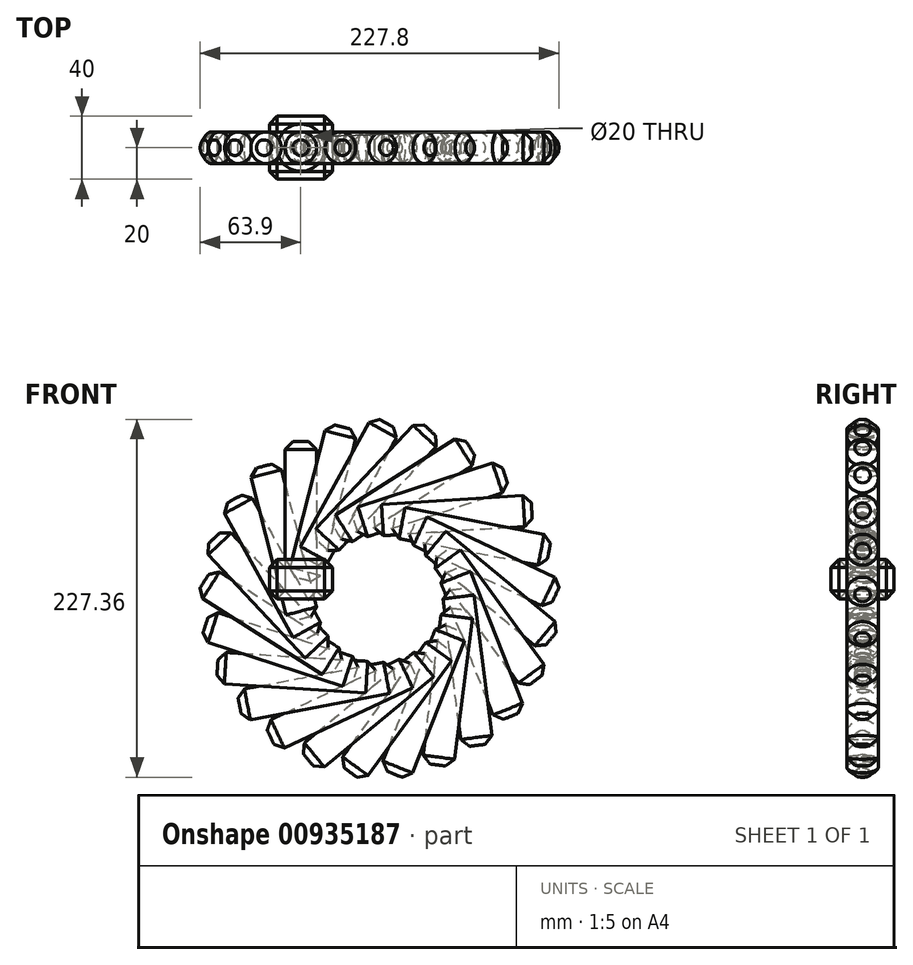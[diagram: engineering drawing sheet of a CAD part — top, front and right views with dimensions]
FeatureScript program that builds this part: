
annotation { "Feature Type Name" : "Feature", "Feature Type Description" : "" }
export const myFeature = defineFeature(function(context is Context, id is Id, definition is map)
    precondition{}
    {
        {
            var Q0;
            Q0=qCreatedBy(makeId("Top.planeOp"),FACE);
            var sketch = newSketch(context, id + "F0", { "sketchPlane" : qUnion([Q0])});
            skLineSegment(sketch, "E0.bottom", {"start": v(20, 20) * mm, "end": v(-20, 20) * mm});
            skLineSegment(sketch, "E0.top", {"start": v(20, -20) * mm, "end": v(-20, -20) * mm});
            skLineSegment(sketch, "E0.left", {"start": v(20, 20) * mm, "end": v(20, -20) * mm});
            skLineSegment(sketch, "E0.right", {"start": v(-20, 20) * mm, "end": v(-20, -20) * mm});
            skPoint(sketch, "E0.middle", {"position": v(0, 0) * mm});
            skCircle(sketch, "E1", {"center": v(0, 0) * mm, "radius": 10 * mm});
            skSolve(sketch);
        }
        {
            var Q0;
            Q0=makeQuery(id+"F0.imprint","IMPRINT",FACE,{"disambiguationData":[TD([[makeQuery(id+"F0.imprint","IMPRINT",EDGE,{"derivedFrom":sQuery(id+"F0.wireOp",EDGE,"E0.bottom")}),1.0]])]});
            extrude(context, id + "F1", {"entities" : qUnion([Q0]), "depth" : 25 * mm, "offsetDistance" : 25 * mm});
        }
        {
            var Q0;
            Q0=makeQuery(id+"F0.imprint","IMPRINT",FACE,{"disambiguationData":[TD([[makeQuery(id+"F0.imprint","IMPRINT",EDGE,{"derivedFrom":sQuery(id+"F0.wireOp",EDGE,"E1")}),1.0]])]});
            extrude(context, id + "F2", {"entities" : qUnion([Q0]), "depth" : 100 * mm, "offsetDistance" : 25 * mm});
        }
        {
            var Q0;
            Q0=makeQuery(id+"F2.opExtrude","CAP_FACE",FACE,{"disambiguationData":[OSD([sQuery(id+"F0.wireOp",EDGE,"E1")])],"isStart":false});
            var Q1;
            Q1=makeQuery(id+"F1.opExtrude","CAP_EDGE",EDGE,{"disambiguationData":[OSD([sQuery(id+"F0.wireOp",EDGE,"E0.bottom")])],"isStart":false});
            var Q2;
            Q2=makeQuery(id+"F1.opExtrude","CAP_EDGE",EDGE,{"disambiguationData":[OSD([sQuery(id+"F0.wireOp",EDGE,"E0.left")])],"isStart":false});
            var Q3;
            Q3=makeQuery(id+"F1.opExtrude","SWEPT_FACE",FACE,{"disambiguationData":[OSD([sQuery(id+"F0.wireOp",EDGE,"E0.bottom")])]});
            var Q4;
            Q4=makeQuery(id+"F1.opExtrude","SWEPT_FACE",FACE,{"disambiguationData":[OSD([sQuery(id+"F0.wireOp",EDGE,"E0.right")])]});
            var Q5;
            Q5=makeQuery(id+"F1.opExtrude","SWEPT_FACE",FACE,{"disambiguationData":[OSD([sQuery(id+"F0.wireOp",EDGE,"E0.top")])]});
            var Q6;
            {var subQ0=sQuery(id+"F0.wireOp",EDGE,"E1");Q6=makeQuery(id+"F2.boolean.opBoolean","MERGE",FACE,{"derivedFrom":[makeQuery(id+"F1.opExtrude","CAP_FACE",FACE,{"disambiguationData":[OSD([sQuery(id+"F0.wireOp",EDGE,"E0.bottom"),sQuery(id+"F0.wireOp",EDGE,"E0.top"),sQuery(id+"F0.wireOp",EDGE,"E0.left"),sQuery(id+"F0.wireOp",EDGE,"E0.right"),subQ0])],"isStart":true}),makeQuery(id+"F2.opExtrude","CAP_FACE",FACE,{"disambiguationData":[OSD([subQ0])],"isStart":true})]});}
            var Q7;
            Q7=makeQuery(id+"F1.opExtrude","CAP_FACE",FACE,{"disambiguationData":[OSD([sQuery(id+"F0.wireOp",EDGE,"E0.bottom"),sQuery(id+"F0.wireOp",EDGE,"E0.top"),sQuery(id+"F0.wireOp",EDGE,"E0.left"),sQuery(id+"F0.wireOp",EDGE,"E0.right"),sQuery(id+"F0.wireOp",EDGE,"E1")])],"isStart":false});
            chamfer(context, id + "F3", {"entities" : qUnion([Q0, Q1, Q2, Q3, Q4, Q5, Q6, Q7]), "width" : 5 * mm, "tangentPropagation" : true});
        }
        {
            var Q0;
            Q0=qCreatedBy(makeId("Front.planeOp"),FACE);
            var sketch = newSketch(context, id + "F4", { "sketchPlane" : qUnion([Q0])});
            skCircle(sketch, "E2", {"center": v(50, 0) * mm, "radius": 20 * mm});
            skSolve(sketch);
        }
        {
            var Q0;
            Q0=makeQuery(id+"F2.opExtrude","SWEPT_BODY",BODY,{"disambiguationData":[OSD([sQuery(id+"F0.wireOp",EDGE,"E1")])]});
            var Q1;
            Q1=sQuery(id+"F4.wireOp",EDGE,"E2");
            circularPattern(context, id + "F5", {"entities" : qUnion([Q0]), "axis" : qUnion([Q1]), "angle" : 360 * degree, "instanceCount" : 25, "equalSpace" : true});
        }
    });
